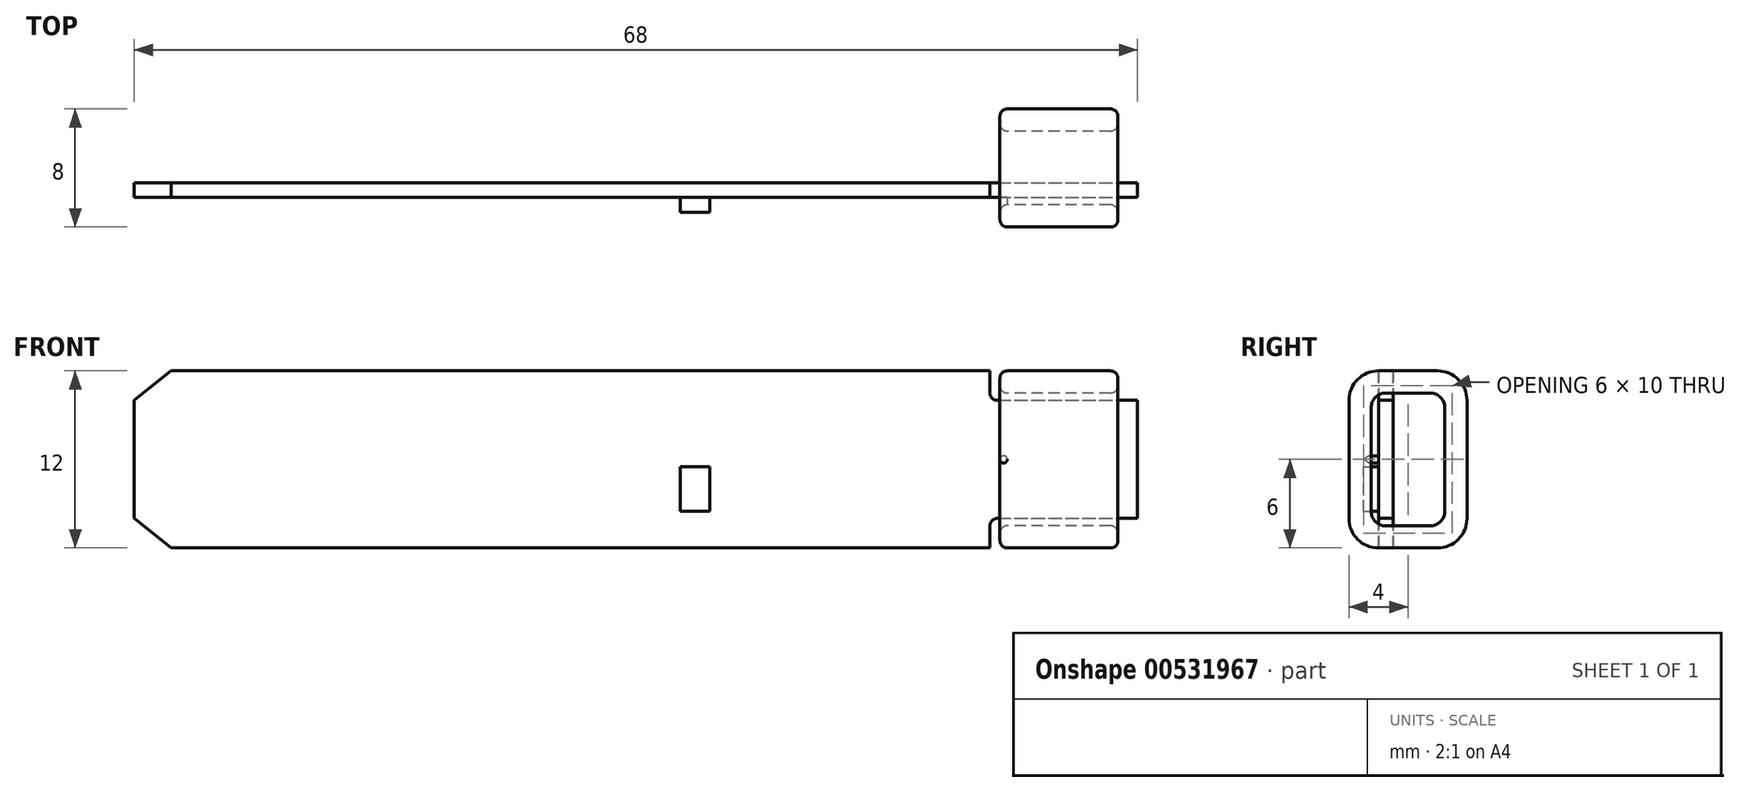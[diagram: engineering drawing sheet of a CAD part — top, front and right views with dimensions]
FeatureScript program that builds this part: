
annotation { "Feature Type Name" : "Feature", "Feature Type Description" : "" }
export const myFeature = defineFeature(function(context is Context, id is Id, definition is map)
    precondition{}
    {
        {
            var Q0;
            Q0=qCreatedBy(makeId("Front.planeOp"),FACE);
            var sketch = newSketch(context, id + "F0", { "sketchPlane" : qUnion([Q0])});
            skLineSegment(sketch, "E0", {"start": v(-42.18, 0) * mm, "end": v(-42.18, 4) * mm});
            skLineSegment(sketch, "E1", {"start": v(-39.68, 6) * mm, "end": v(15.82, 6) * mm});
            skLineSegment(sketch, "E2", {"start": v(15.82, 6) * mm, "end": v(15.82, 4.5) * mm});
            skLineSegment(sketch, "E3", {"start": v(16.32, 4) * mm, "end": v(25.82, 4) * mm});
            skLineSegment(sketch, "E4", {"start": v(25.82, 4) * mm, "end": v(25.82, 0) * mm});
            skPoint(sketch, "E5.visualSharp", {"position": v(15.82, 6) * mm});
            skLineSegment(sketch, "E5.filletArc", {"start": v(15.82, 6) * mm, "end": v(15.82, 6) * mm});
            skPoint(sketch, "E6.visualSharp", {"position": v(15.82, 4) * mm});
            skArc(sketch, "E6.filletArc", {"start": v(15.82, 4.5) * mm, "mid": v(15.97, 4.15) * mm, "end": v(16.32, 4) * mm});
            skPoint(sketch, "E7.visualSharp", {"position": v(25.82, 4) * mm});
            skLineSegment(sketch, "E7.filletArc", {"start": v(25.82, 4) * mm, "end": v(25.82, 4) * mm});
            skLineSegment(sketch, "E8.MirrorCS", {"start": v(-42.18, 0) * mm, "end": v(-42.18, -4) * mm});
            skLineSegment(sketch, "E9.MirrorCS", {"start": v(-39.68, -6) * mm, "end": v(15.82, -6) * mm});
            skLineSegment(sketch, "E10.MirrorCS", {"start": v(15.82, -6) * mm, "end": v(15.82, -4.5) * mm});
            skLineSegment(sketch, "E11.MirrorCS", {"start": v(15.82, -6) * mm, "end": v(15.82, -6) * mm});
            skArc(sketch, "E12.MirrorCS", {"start": v(15.82, -4.5) * mm, "mid": v(15.97, -4.15) * mm, "end": v(16.32, -4) * mm});
            skLineSegment(sketch, "E13.MirrorCS", {"start": v(16.32, -4) * mm, "end": v(25.82, -4) * mm});
            skLineSegment(sketch, "E14.MirrorCS", {"start": v(25.82, -4) * mm, "end": v(25.82, -4) * mm});
            skLineSegment(sketch, "E15.MirrorCS", {"start": v(25.82, -4) * mm, "end": v(25.82, 0) * mm});
            skLineSegment(sketch, "E16", {"start": v(-42.18, 4) * mm, "end": v(-39.68, 6) * mm});
            skLineSegment(sketch, "E17", {"start": v(-42.18, -4) * mm, "end": v(-39.68, -6) * mm});
            skSolve(sketch);
        }
        {
            var Q0;
            Q0=makeQuery(id+"F0.imprint","IMPRINT",FACE,{"disambiguationData":[TD([[makeQuery(id+"F0.imprint","IMPRINT",EDGE,{"derivedFrom":sQuery(id+"F0.wireOp",EDGE,"E0")}),-1.0]])]});
            extrude(context, id + "F1", {"entities" : qUnion([Q0]), "depth" : 1 * mm});
        }
        {
            var Q0;
            Q0=qCreatedBy(makeId("Right.planeOp"),FACE);
            cPlane(context, id + "F2", {"entities" : qUnion([Q0]), "cplaneType" : CPlaneType.OFFSET, "offset" : 16.5 * mm, "width" : 150 * mm, "height" : 150 * mm});
        }
        {
            var Q0;
            Q0=qCreatedBy(id+"F2.planeOp",FACE);
            var sketch = newSketch(context, id + "F3", { "sketchPlane" : qUnion([Q0])});
            skLineSegment(sketch, "E18.bottom", {"start": v(3, -6) * mm, "end": v(-1, -6) * mm});
            skLineSegment(sketch, "E18.top", {"start": v(3, 6) * mm, "end": v(-1, 6) * mm});
            skLineSegment(sketch, "E18.left", {"start": v(5, -4) * mm, "end": v(5, 4) * mm});
            skLineSegment(sketch, "E18.right", {"start": v(-3, -4) * mm, "end": v(-3, 4) * mm});
            skPoint(sketch, "E18.middle", {"position": v(0, 0) * mm});
            skPoint(sketch, "E19.visualSharp", {"position": v(-3, 6) * mm});
            skArc(sketch, "E19.filletArc", {"start": v(-1, 6) * mm, "mid": v(-2.41, 5.41) * mm, "end": v(-3, 4) * mm});
            skPoint(sketch, "E20.visualSharp", {"position": v(5, 6) * mm});
            skArc(sketch, "E20.filletArc", {"start": v(5, 4) * mm, "mid": v(4.41, 5.41) * mm, "end": v(3, 6) * mm});
            skPoint(sketch, "E21.visualSharp", {"position": v(-3, -6) * mm});
            skArc(sketch, "E21.filletArc", {"start": v(-3, -4) * mm, "mid": v(-2.41, -5.41) * mm, "end": v(-1, -6) * mm});
            skPoint(sketch, "E22.visualSharp", {"position": v(5, -6) * mm});
            skArc(sketch, "E22.filletArc", {"start": v(3, -6) * mm, "mid": v(4.41, -5.41) * mm, "end": v(5, -4) * mm});
            skLineSegment(sketch, "E23.bottom", {"start": v(2.5, -4.5) * mm, "end": v(-0.5, -4.5) * mm});
            skLineSegment(sketch, "E23.top", {"start": v(2.5, 4.5) * mm, "end": v(-0.5, 4.5) * mm});
            skLineSegment(sketch, "E23.left", {"start": v(3.5, -3.5) * mm, "end": v(3.5, 3.5) * mm});
            skLineSegment(sketch, "E23.right", {"start": v(-1.5, -3.5) * mm, "end": v(-1.5, 3.5) * mm});
            skPoint(sketch, "E24.visualSharp", {"position": v(-1.5, 4.5) * mm});
            skArc(sketch, "E24.filletArc", {"start": v(-0.5, 4.5) * mm, "mid": v(-1.2, 4.2) * mm, "end": v(-1.5, 3.5) * mm});
            skPoint(sketch, "E25.visualSharp", {"position": v(3.5, 4.5) * mm});
            skArc(sketch, "E25.filletArc", {"start": v(3.5, 3.5) * mm, "mid": v(3.2, 4.2) * mm, "end": v(2.5, 4.5) * mm});
            skPoint(sketch, "E26.visualSharp", {"position": v(-1.5, -4.5) * mm});
            skArc(sketch, "E26.filletArc", {"start": v(-1.5, -3.5) * mm, "mid": v(-1.2, -4.2) * mm, "end": v(-0.5, -4.5) * mm});
            skPoint(sketch, "E27.visualSharp", {"position": v(3.5, -4.5) * mm});
            skArc(sketch, "E27.filletArc", {"start": v(2.5, -4.5) * mm, "mid": v(3.2, -4.2) * mm, "end": v(3.5, -3.5) * mm});
            skSolve(sketch);
        }
        {
            var Q0;
            Q0=qSketchRegion(id+"F3",true);
            extrude(context, id + "F4", {"entities" : qUnion([Q0]), "operationType" : NewBodyOperationType.ADD, "depth" : 8 * mm, "offsetDistance" : 25 * mm});
        }
        {
            var Q0;
            Q0=makeQuery(id+"F4.opExtrude","CAP_EDGE",EDGE,{"disambiguationData":[OSD([sQuery(id+"F3.wireOp",EDGE,"E19.filletArc")])],"isStart":false});
            var Q1;
            Q1=makeQuery(id+"F4.opExtrude","CAP_EDGE",EDGE,{"disambiguationData":[OSD([sQuery(id+"F3.wireOp",EDGE,"E24.filletArc")])],"isStart":false});
            var Q2;
            Q2=makeQuery(id+"F4.opExtrude","CAP_EDGE",EDGE,{"disambiguationData":[OSD([sQuery(id+"F3.wireOp",EDGE,"E24.filletArc")])],"isStart":true});
            var Q3;
            Q3=makeQuery(id+"F4.opExtrude","CAP_EDGE",EDGE,{"disambiguationData":[OSD([sQuery(id+"F3.wireOp",EDGE,"E19.filletArc")])],"isStart":true});
            fillet(context, id + "F5", {"entities" : qUnion([Q0, Q1, Q2, Q3]), "radius" : 0.5 * mm, "tangentPropagation" : true, "allowEdgeOverflow" : false});
        }
        {
            var Q0;
            Q0=qCreatedBy(id+"F2.planeOp",FACE);
            var sketch = newSketch(context, id + "F6", { "sketchPlane" : qUnion([Q0])});
            skLineSegment(sketch, "E28.bottom", {"start": v(-0.16, -0.25) * mm, "end": v(-2.16, -0.25) * mm});
            skLineSegment(sketch, "E28.top", {"start": v(-0.16, 0.25) * mm, "end": v(-2.16, 0.25) * mm});
            skLineSegment(sketch, "E28.left", {"start": v(-0.16, -0.25) * mm, "end": v(-0.16, 0.25) * mm});
            skLineSegment(sketch, "E28.right", {"start": v(-2.16, -0.25) * mm, "end": v(-2.16, 0.25) * mm});
            skPoint(sketch, "E28.middle", {"position": v(-1.16, 0) * mm});
            skSolve(sketch);
        }
        {
            var Q0;
            Q0=qSketchRegion(id+"F6",true);
            extrude(context, id + "F7", {"entities" : qUnion([Q0]), "operationType" : NewBodyOperationType.ADD, "depth" : 0.5 * mm, "offsetDistance" : 25 * mm});
        }
        {
            var Q0;
            Q0=makeQuery(id+"F7.opExtrude","CAP_EDGE",EDGE,{"disambiguationData":[OSD([sQuery(id+"F6.wireOp",EDGE,"E28.top")])],"isStart":false});
            var Q1;
            Q1=makeQuery(id+"F7.opExtrude","CAP_EDGE",EDGE,{"disambiguationData":[OSD([sQuery(id+"F6.wireOp",EDGE,"E28.bottom")])],"isStart":false});
            var Q2;
            Q2=makeQuery(id+"F7.opExtrude","CAP_EDGE",EDGE,{"disambiguationData":[OSD([sQuery(id+"F6.wireOp",EDGE,"E28.bottom")])],"isStart":true});
            var Q3;
            Q3=makeQuery(id+"F7.opExtrude","CAP_EDGE",EDGE,{"disambiguationData":[OSD([sQuery(id+"F6.wireOp",EDGE,"E28.top")])],"isStart":true});
            fillet(context, id + "F8", {"entities" : qUnion([Q0, Q1, Q2, Q3]), "radius" : 0.25 * mm, "tangentPropagation" : true, "allowEdgeOverflow" : false});
        }
        {
            var Q0;
            Q0=qCreatedBy(makeId("Front.planeOp"),FACE);
            var sketch = newSketch(context, id + "F9", { "sketchPlane" : qUnion([Q0])});
            skLineSegment(sketch, "E29.bottom", {"start": v(-3.18, -3.5) * mm, "end": v(-5.18, -3.5) * mm});
            skLineSegment(sketch, "E29.top", {"start": v(-3.18, -0.5) * mm, "end": v(-5.18, -0.5) * mm});
            skLineSegment(sketch, "E29.left", {"start": v(-3.18, -3.5) * mm, "end": v(-3.18, -0.5) * mm});
            skLineSegment(sketch, "E29.right", {"start": v(-5.18, -3.5) * mm, "end": v(-5.18, -0.5) * mm});
            skSolve(sketch);
        }
        {
            var Q0;
            Q0=qSketchRegion(id+"F9",true);
            extrude(context, id + "F10", {"entities" : qUnion([Q0]), "operationType" : NewBodyOperationType.ADD, "depth" : 2 * mm, "offsetDistance" : 25 * mm});
        }
    });
